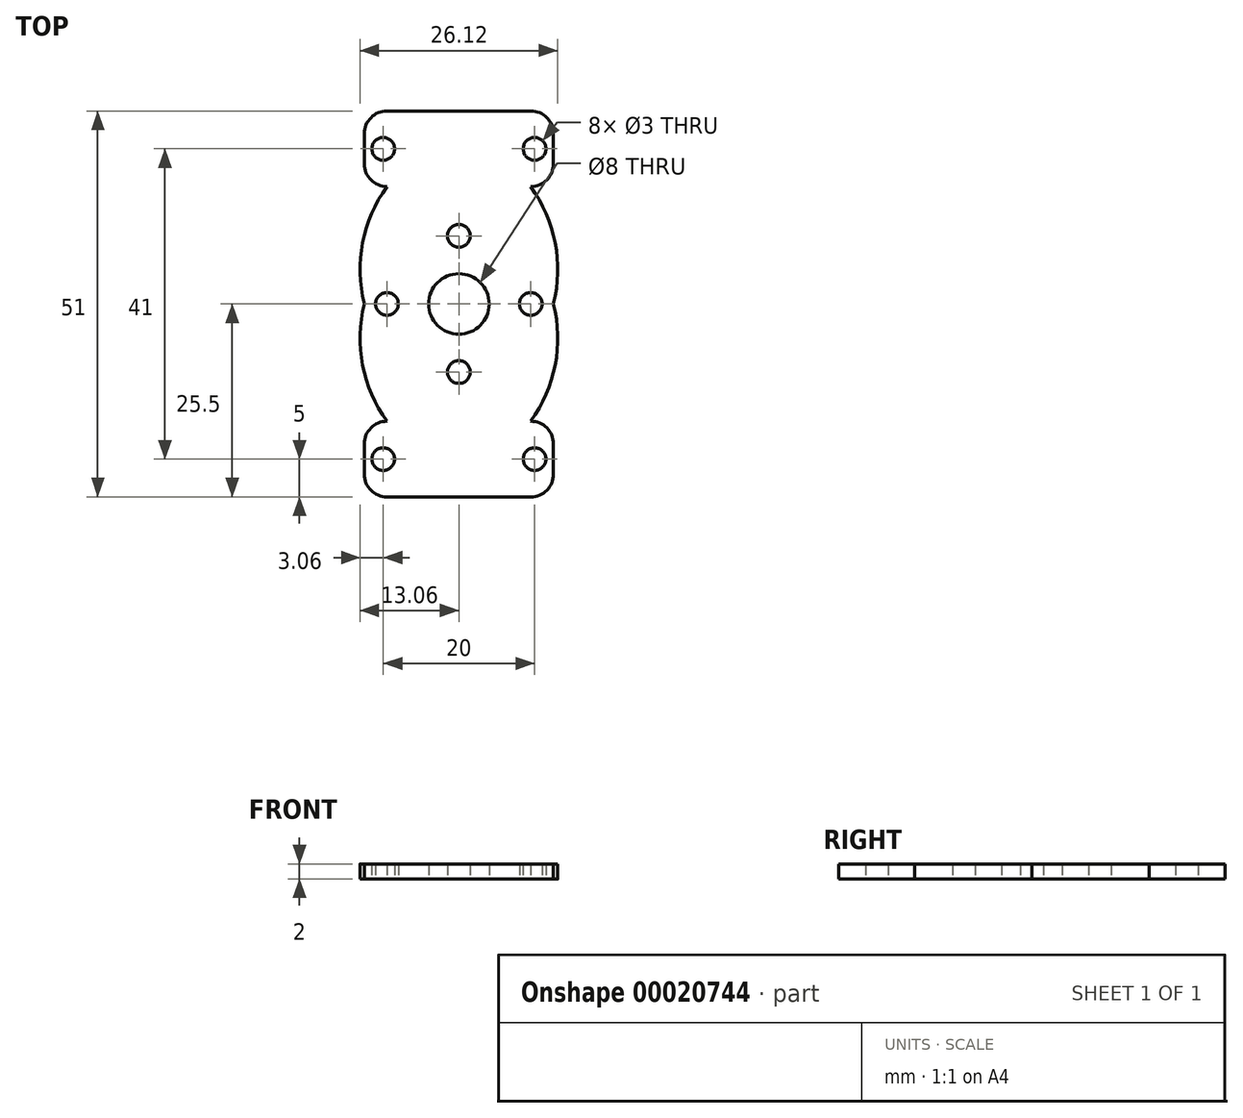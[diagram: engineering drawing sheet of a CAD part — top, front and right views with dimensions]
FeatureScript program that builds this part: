
annotation { "Feature Type Name" : "Feature", "Feature Type Description" : "" }
export const myFeature = defineFeature(function(context is Context, id is Id, definition is map)
    precondition{}
    {
        {
            var Q0;
            Q0=qCreatedBy(makeId("Top.planeOp"),FACE);
            var sketch = newSketch(context, id + "F0", { "sketchPlane" : qUnion([Q0])});
            skCircle(sketch, "E0", {"center": v(0, 9) * mm, "radius": 1.5 * mm});
            skCircle(sketch, "E1", {"center": v(9.5, 0) * mm, "radius": 1.5 * mm});
            skCircle(sketch, "E2", {"center": v(0, -9) * mm, "radius": 1.5 * mm});
            skCircle(sketch, "E3", {"center": v(-9.5, 0) * mm, "radius": 1.5 * mm});
            skLineSegment(sketch, "E4.rect.top", {"start": v(9.5, -25.5) * mm, "end": v(-9.5, -25.5) * mm});
            skLineSegment(sketch, "E4.rect.left", {"start": v(12.5, -18.5) * mm, "end": v(12.5, -22.5) * mm});
            skLineSegment(sketch, "E4.rect.right", {"start": v(-12.5, -18.5) * mm, "end": v(-12.5, -22.5) * mm});
            skPoint(sketch, "E4.rect.middle", {"position": v(0, -20.5) * mm});
            skArc(sketch, "E5.filletArc", {"start": v(12.5, -18.5) * mm, "mid": v(11.62, -16.38) * mm, "end": v(9.5, -15.5) * mm});
            skArc(sketch, "E6.filletArc", {"start": v(9.5, -25.5) * mm, "mid": v(11.62, -24.62) * mm, "end": v(12.5, -22.5) * mm});
            skArc(sketch, "E7.filletArc", {"start": v(-12.5, -22.5) * mm, "mid": v(-11.62, -24.62) * mm, "end": v(-9.5, -25.5) * mm});
            skArc(sketch, "E8.filletArc", {"start": v(-9.5, -15.5) * mm, "mid": v(-11.62, -16.38) * mm, "end": v(-12.5, -18.5) * mm});
            skCircle(sketch, "E9", {"center": v(0, 0) * mm, "radius": 4 * mm});
            skCircle(sketch, "E10", {"center": v(10, -20.5) * mm, "radius": 1.5 * mm});
            skCircle(sketch, "E11.MirrorC", {"center": v(-10, -20.5) * mm, "radius": 1.5 * mm});
            skArc(sketch, "E12", {"start": v(-12.5, 0) * mm, "mid": v(-12.72, -8.08) * mm, "end": v(-9.5, -15.5) * mm});
            skArc(sketch, "E13.MirrorCS", {"start": v(12.5, 0) * mm, "mid": v(12.72, -8.08) * mm, "end": v(9.5, -15.5) * mm});
            skArc(sketch, "E14.MirrorCS", {"start": v(12.5, 0) * mm, "mid": v(12.72, 8.08) * mm, "end": v(9.5, 15.5) * mm});
            skArc(sketch, "E15.MirrorCS", {"start": v(-12.5, 0) * mm, "mid": v(-12.72, 8.08) * mm, "end": v(-9.5, 15.5) * mm});
            skArc(sketch, "E16.MirrorCS", {"start": v(12.5, 18.5) * mm, "mid": v(11.62, 16.38) * mm, "end": v(9.5, 15.5) * mm});
            skLineSegment(sketch, "E17.MirrorCS", {"start": v(12.5, 18.5) * mm, "end": v(12.5, 22.5) * mm});
            skArc(sketch, "E18.MirrorCS", {"start": v(9.5, 25.5) * mm, "mid": v(11.62, 24.62) * mm, "end": v(12.5, 22.5) * mm});
            skLineSegment(sketch, "E19.MirrorCS", {"start": v(9.5, 25.5) * mm, "end": v(-9.5, 25.5) * mm});
            skArc(sketch, "E20.MirrorCS", {"start": v(-12.5, 22.5) * mm, "mid": v(-11.62, 24.62) * mm, "end": v(-9.5, 25.5) * mm});
            skLineSegment(sketch, "E21.MirrorCS", {"start": v(-12.5, 18.5) * mm, "end": v(-12.5, 22.5) * mm});
            skArc(sketch, "E22.MirrorCS", {"start": v(-9.5, 15.5) * mm, "mid": v(-11.62, 16.38) * mm, "end": v(-12.5, 18.5) * mm});
            skCircle(sketch, "E23.MirrorC", {"center": v(-10, 20.5) * mm, "radius": 1.5 * mm});
            skCircle(sketch, "E24.MirrorC", {"center": v(10, 20.5) * mm, "radius": 1.5 * mm});
            skSolve(sketch);
        }
        {
            var Q0;
            Q0=makeQuery(id+"F0.imprint","IMPRINT",FACE,{"disambiguationData":[TD([[makeQuery(id+"F0.imprint","IMPRINT",EDGE,{"derivedFrom":sQuery(id+"F0.wireOp",EDGE,"9c67296d-28cd-4141-8f30-57d821963a36")}),1.0]])]});
            var Q1;
            Q1=makeQuery(id+"F0.imprint","IMPRINT",FACE,{"disambiguationData":[TD([[makeQuery(id+"F0.imprint","IMPRINT",EDGE,{"derivedFrom":sQuery(id+"F0.wireOp",EDGE,"E4.rect.top")}),-1.0]])]});
            extrude(context, id + "F1", {"entities" : qUnion([Q0, Q1]), "depth" : 2 * mm});
        }
    });
